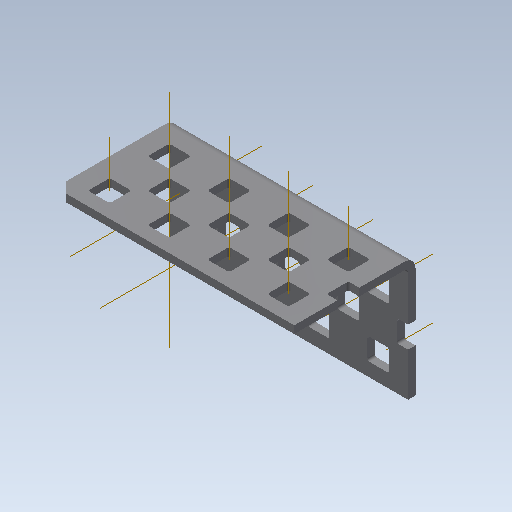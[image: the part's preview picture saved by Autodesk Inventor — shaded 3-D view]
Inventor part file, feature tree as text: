
AUTODESK INVENTOR PART (.ipt)
format: ipt  version: 2020 (Build 240168000, 168)  size: 1,832,960 bytes
history: native  units: in
note: dims shown in document units (in); Inventor stores cm internally (conversion verified against a paired STEP export)
features: other x29, pattern_linear x4, sheet_metal_op x1, extrude x1, imported_body x1, sketch x1
ambient origin geometry x8: Origin, YZ Plane, XZ Plane, XY Plane, X Axis, Y Axis, Z Axis, Center Point
bodies: Body1 (feature_tree)
feature tree (37):
  sheet_metal_op  "Fold1"
  other  "L-Channel"
  extrude  "length cut"  Depth=0.5in
  other  "top out axis"
  other  "top inner axis"
  other  "back out axis"
  other  "back inner axis"
  pattern_linear  "top outer axes"  Count1=2 Spacing1=0.5in
  pattern_linear  "top inner axes"  Spacing1=0.5in  [1 undecoded]
  pattern_linear  "back outer axes"  Count1=2 Spacing1=0.5in
  pattern_linear  "back inner axes"  Spacing1=0.5in  [1 undecoded]
  other  "right plane"
  imported_body  "Base1"
  sketch  "Sketch1"  dims[d1=0.0in d4=0.5in d5=0.7874in d7=0.5in d10=0.5in d13=0.5in d14=0.7874in d16=0.5in d19=0.5in d20=-2.0in d21=0.0in d22=0.0in d23=0.0in d24=0.0in d25=0.0in d26=0.0in]
  other  "Work Point1"
  other  "Work Point2"
  other  "Work Point3"
  other  "Work Point4"
  other  "Work Axis5"
  other  "Work Axis6"
  other  "Work Axis7"
  other  "Work Axis11"
  other  "Work Axis12"
  other  "Work Axis13"
  other  "Work Axis14"
  other  "Work Axis18"
  other  "Work Axis19"
  other  "Work Axis23"
  other  "Work Axis24"
  other  "Work Axis25"
  other  "Work Axis29"
  other  "Work Axis30"
  other  "Work Axis31"
  other  "Work Axis32"
  other  "Work Axis36"
  other  "Work Axis37"
  other  "left plane"
note: 2 required parameter values undecoded (feature->parameter linkage not recoverable at this tier; creation-order binding heuristic only, values carry confidence <= 0.55)
